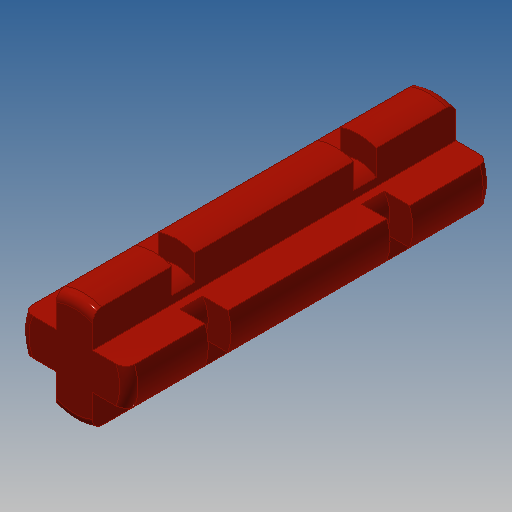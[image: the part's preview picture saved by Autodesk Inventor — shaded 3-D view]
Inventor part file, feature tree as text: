
AUTODESK INVENTOR PART (.ipt)
format: ipt  version: 2022.2 (Build 262287000, 287)  size: 196,096 bytes
history: native  units: in
note: dims shown in document units (in); Inventor stores cm internally (conversion verified against a paired STEP export)
features: sketch x2, extrude x1, fillet x1, revolve x1
ambient origin geometry x8: Origin, YZ Plane, XZ Plane, XY Plane, X Axis, Y Axis, Z Axis, Center Point
bodies: Solid1 (feature_tree)
feature tree (5):
  extrude  "Extrusion1"  Depth=0.063in
  fillet  "Fillet1"  Radius=0.6299in
  revolve  "Revolution1"  [1 undecoded]
  sketch  "Sketch1"  dims[d0=0.189in d1=0.063in d2=0.6299in]
  sketch  "Sketch2"  dims[d3=0.0in d4=0.0157in d5=0.0in d6=0.0in d7=0.315in d8=0.0394in d9=90.0deg d10=0.0in]
note: 1 required parameter value undecoded (feature->parameter linkage not recoverable at this tier; creation-order binding heuristic only, values carry confidence <= 0.55)
